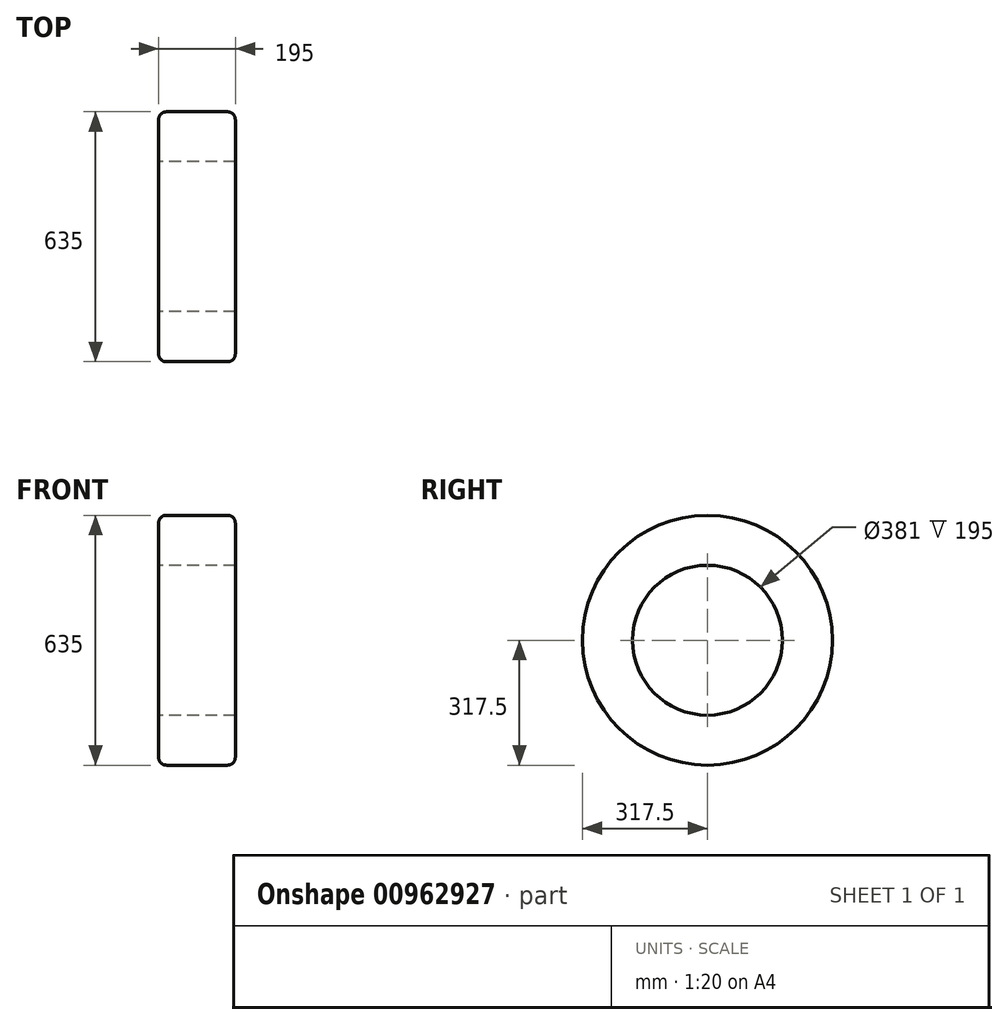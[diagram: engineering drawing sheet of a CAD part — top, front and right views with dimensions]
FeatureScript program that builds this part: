
annotation { "Feature Type Name" : "Feature", "Feature Type Description" : "" }
export const myFeature = defineFeature(function(context is Context, id is Id, definition is map)
    precondition{}
    {
        {
            var Q0;
            Q0=qCreatedBy(makeId("Right.planeOp"),FACE);
            var sketch = newSketch(context, id + "F0", { "sketchPlane" : qUnion([Q0])});
            skCircle(sketch, "E0", {"center": v(0, 0) * mm, "radius": 190.5 * mm});
            skCircle(sketch, "E1", {"center": v(0, 0) * mm, "radius": 317.5 * mm});
            skSolve(sketch);
        }
        {
            var Q0;
            Q0=makeQuery(id+"F0.imprint","IMPRINT",FACE,{"disambiguationData":[TD([[makeQuery(id+"F0.imprint","IMPRINT",EDGE,{"derivedFrom":sQuery(id+"F0.wireOp",EDGE,"E0")}),-1.0]])]});
            extrude(context, id + "F1", {"entities" : qUnion([Q0]), "endBound" : BoundingType.SYMMETRIC, "depth" : 195 * mm, "offsetDistance" : 25 * mm});
        }
        {
            var Q0;
            Q0=makeQuery(id+"F1.opExtrude","CAP_EDGE",EDGE,{"disambiguationData":[OSD([sQuery(id+"F0.wireOp",EDGE,"E1")])],"isStart":false});
            var Q1;
            Q1=makeQuery(id+"F1.opExtrude","CAP_EDGE",EDGE,{"disambiguationData":[OSD([sQuery(id+"F0.wireOp",EDGE,"E1")])],"isStart":true});
            fillet(context, id + "F2", {"entities" : qUnion([Q0, Q1]), "radius" : 20 * mm, "tangentPropagation" : true, "allowEdgeOverflow" : false});
        }
    });
